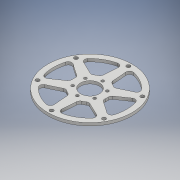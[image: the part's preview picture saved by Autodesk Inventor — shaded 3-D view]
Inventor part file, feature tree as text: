
AUTODESK INVENTOR PART (.ipt)
format: ipt  version: 2019.3 (Build 233278000, 278)  size: 197,120 bytes
history: native  units: mm
features: sketch x2, extrude x2, hole x2, other x1, fillet x1, pattern_circular x1
ambient origin geometry x8: Origin, YZ Plane, XZ Plane, XY Plane, X Axis, Y Axis, Z Axis, Center Point
bodies: Body1 (feature_tree)
feature tree (9):
  other  "SprocketHubPlate"
  sketch  "Sketch1"  dims[d0=66.675mm d1=60.0mm d3=360.0deg]
  extrude  "Extrusion2"  Depth=60.0mm TaperAngle=360.0deg
  hole  "Hole2"  [1 undecoded]
  hole  "Hole3"  [1 undecoded]
  extrude  "Extrusion4"  Depth=6.0mm
  fillet  "Fillet1"  Radius=5.0mm
  pattern_circular  "Circular Pattern1"  [2 undecoded]
  sketch  "Sketch4"  dims[d9=33.0mm d20=22.0mm d21=60.0mm d23=360.0deg d25=146.0mm d30=5.0mm d31=0.0mm d32=6.5mm d33=6.0mm d34=4.0mm d35=2.0mm d36=90.0deg d37=8.0mm d38=20.594885mm d39=5.0mm d40=6.0mm d41=4.0mm d42=2.0mm d43=90.0deg d44=8.0mm d45=20.594885mm d46=62.0mm d60=7.0mm d61=7.0mm d62=10.0mm d63=0.0mm d64=6.0mm d65=60.0mm d66=360.0deg d12=1.0mm d13=1.0mm]
note: 4 required parameter values undecoded (feature->parameter linkage not recoverable at this tier; creation-order binding heuristic only, values carry confidence <= 0.55)
